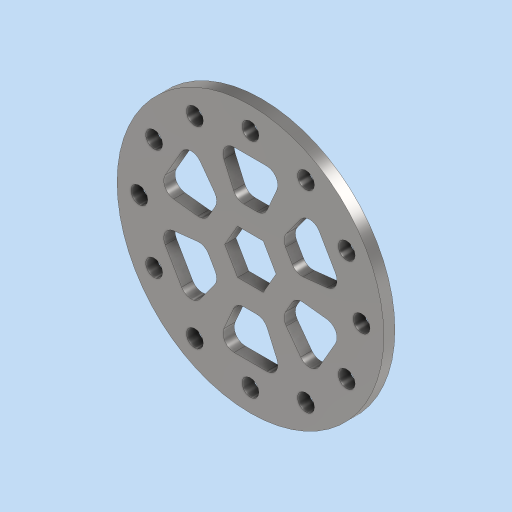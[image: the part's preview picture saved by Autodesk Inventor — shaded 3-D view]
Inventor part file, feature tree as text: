
AUTODESK INVENTOR PART (.ipt)
format: ipt  version: 2023 (Build 270158000, 158)  size: 224,768 bytes
history: native  units: in
note: dims shown in document units (in); Inventor stores cm internally (conversion verified against a paired STEP export)
features: extrude x2, sketch x1, fillet x1, pattern_circular x1
ambient origin geometry x8: Origin, YZ Plane, XZ Plane, XY Plane, X Axis, Y Axis, Z Axis, Center Point
bodies: Solid1 (feature_tree)
feature tree (5):
  sketch  "Sketch1"  dims[d0=3.0in d1=0.5in d2=2.5in d3=0.19in d4=4.7244in d6=360.0deg d8=0.125in d9=0.0in d10=0.125in d11=0.0in d12=0.125in d13=2.3622in d14=360.0deg d16=0.25in d18=0.3125in d19=0.75in d20=0.5in]
  extrude  "Extrusion1"  Depth=0.5in
  extrude  "Extrusion2"  Depth=0.5in
  fillet  "Fillet1"  Radius=0.19in
  pattern_circular  "Circular Pattern1"  Count=12 Angle=360.0deg
